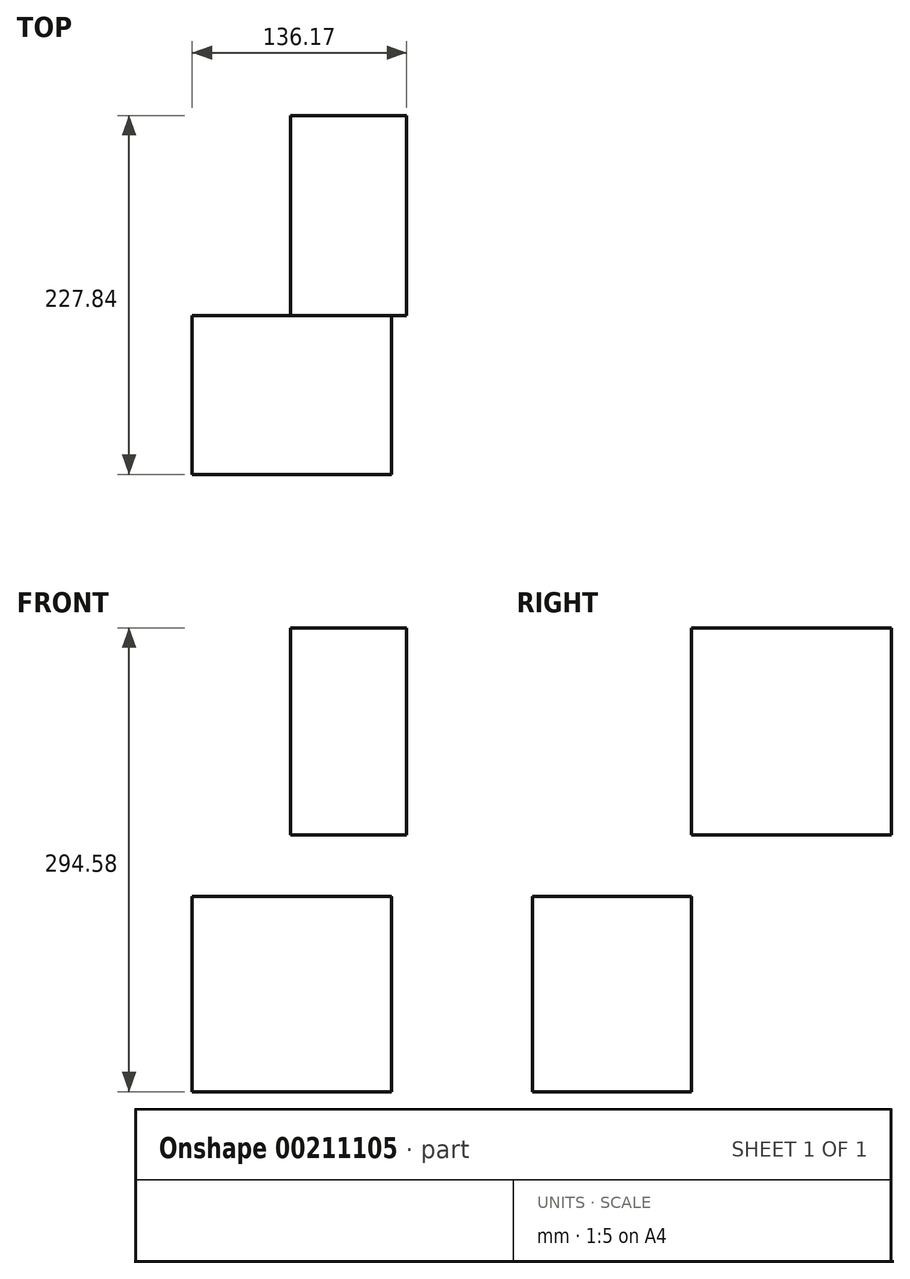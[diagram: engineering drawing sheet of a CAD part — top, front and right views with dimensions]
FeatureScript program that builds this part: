
annotation { "Feature Type Name" : "Feature", "Feature Type Description" : "" }
export const myFeature = defineFeature(function(context is Context, id is Id, definition is map)
    precondition{}
    {
        {
            var Q0;
            Q0=qCreatedBy(makeId("Front.planeOp"),FACE);
            var sketch = newSketch(context, id + "F0", { "sketchPlane" : qUnion([Q0])});
            skLineSegment(sketch, "E0.bottom", {"start": v(-62.5, 59.97) * mm, "end": v(64, 59.97) * mm});
            skLineSegment(sketch, "E0.top", {"start": v(-62.5, -64.03) * mm, "end": v(64, -64.03) * mm});
            skLineSegment(sketch, "E0.left", {"start": v(-62.5, 59.97) * mm, "end": v(-62.5, -64.03) * mm});
            skLineSegment(sketch, "E0.right", {"start": v(64, 59.97) * mm, "end": v(64, -64.03) * mm});
            skSolve(sketch);
        }
        {
            var Q0;
            Q0=qCreatedBy(makeId("Right.planeOp"),FACE);
            var sketch = newSketch(context, id + "F1", { "sketchPlane" : qUnion([Q0])});
            skLineSegment(sketch, "E1.bottom", {"start": v(0, 230.55) * mm, "end": v(127, 230.55) * mm});
            skLineSegment(sketch, "E1.top", {"start": v(0, 99.02) * mm, "end": v(127, 99.02) * mm});
            skLineSegment(sketch, "E1.left", {"start": v(0, 230.55) * mm, "end": v(0, 99.02) * mm});
            skLineSegment(sketch, "E1.right", {"start": v(127, 230.55) * mm, "end": v(127, 99.02) * mm});
            skSolve(sketch);
        }
        {
            var Q0;
            Q0=makeQuery(id+"F1.imprint","IMPRINT",FACE,{"disambiguationData":[TD([[makeQuery(id+"F1.imprint","IMPRINT",EDGE,{"derivedFrom":sQuery(id+"F1.wireOp",EDGE,"E1.bottom")}),-1.0]])]});
            extrude(context, id + "F2", {"entities" : qUnion([Q0]), "depth" : 73.66 * mm});
        }
        {
            var Q0;
            Q0=makeQuery(id+"F0.imprint","IMPRINT",FACE,{"disambiguationData":[TD([[makeQuery(id+"F0.imprint","IMPRINT",EDGE,{"derivedFrom":sQuery(id+"F0.wireOp",EDGE,"E0.bottom")}),-1.0]])]});
            extrude(context, id + "F3", {"entities" : qUnion([Q0]), "depth" : 100.84 * mm});
        }
    });
